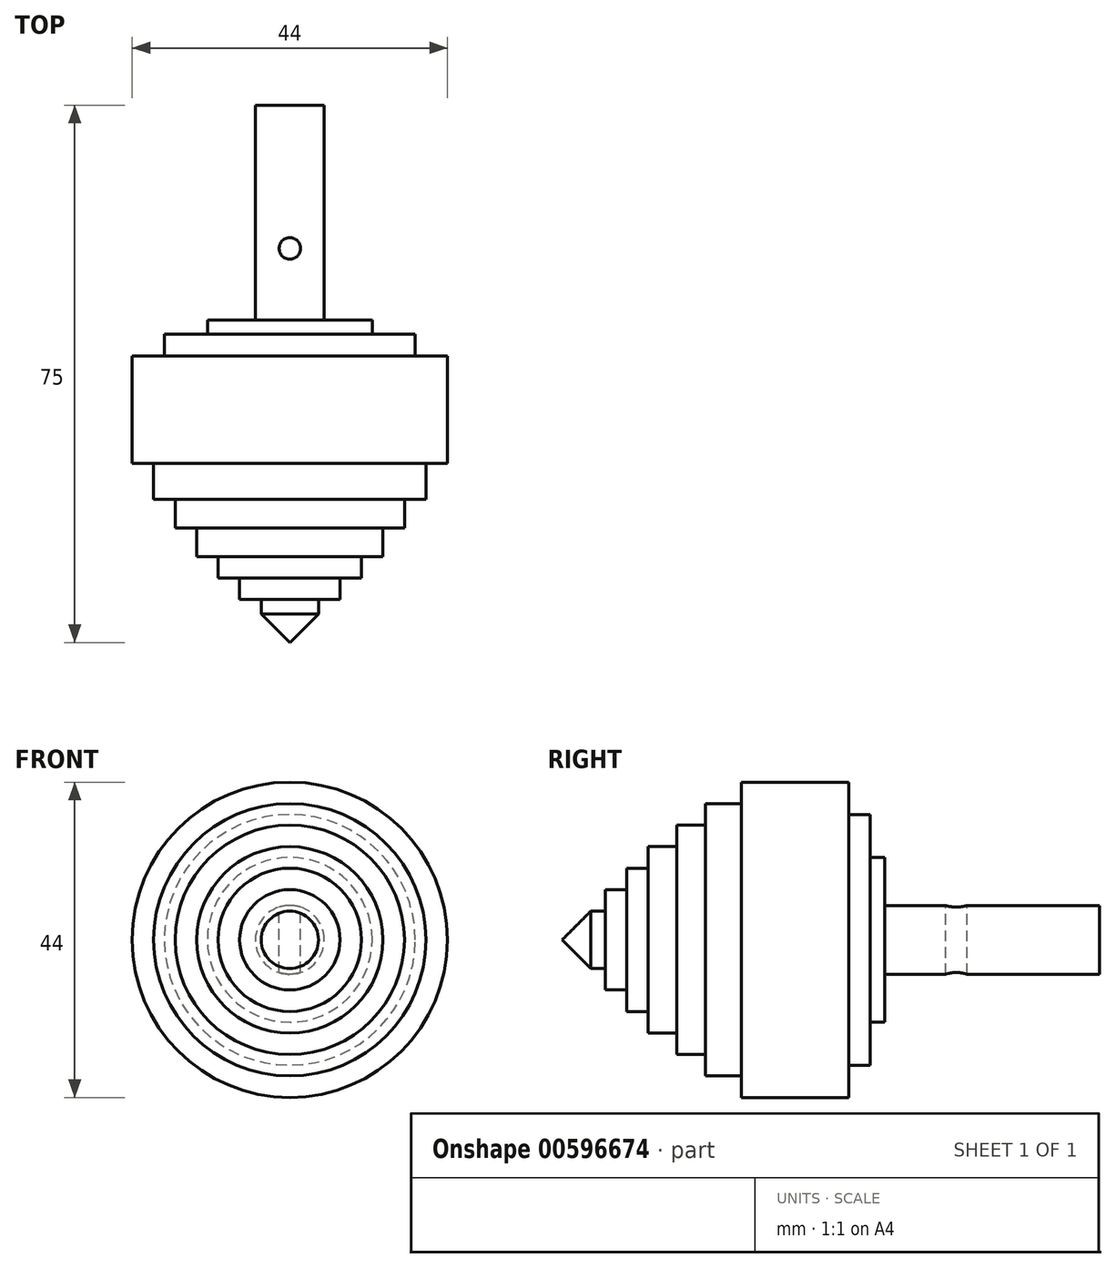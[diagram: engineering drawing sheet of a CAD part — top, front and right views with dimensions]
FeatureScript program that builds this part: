
annotation { "Feature Type Name" : "Feature", "Feature Type Description" : "" }
export const myFeature = defineFeature(function(context is Context, id is Id, definition is map)
    precondition{}
    {
        {
            var Q0;
            Q0=qCreatedBy(makeId("Front.planeOp"),FACE);
            var sketch = newSketch(context, id + "F0", { "sketchPlane" : qUnion([Q0])});
            skCircle(sketch, "E0", {"center": v(0, 0) * mm, "radius": 22 * mm});
            skCircle(sketch, "E1", {"center": v(0, 0) * mm, "radius": 19 * mm});
            skCircle(sketch, "E2", {"center": v(0, 0) * mm, "radius": 16 * mm});
            skCircle(sketch, "E3", {"center": v(0, 0) * mm, "radius": 13 * mm});
            skCircle(sketch, "E4", {"center": v(0, 0) * mm, "radius": 10 * mm});
            skCircle(sketch, "E5", {"center": v(0, 0) * mm, "radius": 7 * mm});
            skCircle(sketch, "E6", {"center": v(0, 0) * mm, "radius": 4 * mm});
            skSolve(sketch);
        }
        {
            var Q0;
            Q0 = qSketchRegion(id + "F0", true);
            var Q1;
            Q1=makeQuery(id+"F0.imprint","IMPRINT",FACE,{"disambiguationData":[TD([[makeQuery(id+"F0.imprint","IMPRINT",EDGE,{"derivedFrom":sQuery(id+"F0.wireOp",EDGE,"E1")}),1.0]])]});
            var Q2;
            Q2=makeQuery(id+"F0.imprint","IMPRINT",FACE,{"disambiguationData":[TD([[makeQuery(id+"F0.imprint","IMPRINT",EDGE,{"derivedFrom":sQuery(id+"F0.wireOp",EDGE,"E2")}),1.0]])]});
            var Q3;
            Q3=makeQuery(id+"F0.imprint","IMPRINT",FACE,{"disambiguationData":[TD([[makeQuery(id+"F0.imprint","IMPRINT",EDGE,{"derivedFrom":sQuery(id+"F0.wireOp",EDGE,"E3")}),1.0]])]});
            var Q4;
            Q4=makeQuery(id+"F0.imprint","IMPRINT",FACE,{"disambiguationData":[TD([[makeQuery(id+"F0.imprint","IMPRINT",EDGE,{"derivedFrom":sQuery(id+"F0.wireOp",EDGE,"E4")}),1.0]])]});
            var Q5;
            Q5=makeQuery(id+"F0.imprint","IMPRINT",FACE,{"disambiguationData":[TD([[makeQuery(id+"F0.imprint","IMPRINT",EDGE,{"derivedFrom":sQuery(id+"F0.wireOp",EDGE,"E5")}),1.0]])]});
            var Q6;
            Q6=makeQuery(id+"F0.imprint","IMPRINT",FACE,{"disambiguationData":[TD([[makeQuery(id+"F0.imprint","IMPRINT",EDGE,{"derivedFrom":sQuery(id+"F0.wireOp",EDGE,"E6")}),1.0]])]});
            extrude(context, id + "F1", {"entities" : qUnion([Q0, Q1, Q2, Q3, Q4, Q5, Q6]), "depth" : 15 * mm, "offsetDistance" : 25 * mm});
        }
        {
            var Q0;
            Q0=makeQuery(id+"F0.imprint","IMPRINT",FACE,{"disambiguationData":[TD([[makeQuery(id+"F0.imprint","IMPRINT",EDGE,{"derivedFrom":sQuery(id+"F0.wireOp",EDGE,"E1")}),1.0]])]});
            var Q1;
            Q1=makeQuery(id+"F0.imprint","IMPRINT",FACE,{"disambiguationData":[TD([[makeQuery(id+"F0.imprint","IMPRINT",EDGE,{"derivedFrom":sQuery(id+"F0.wireOp",EDGE,"E2")}),1.0]])]});
            var Q2;
            Q2=makeQuery(id+"F0.imprint","IMPRINT",FACE,{"disambiguationData":[TD([[makeQuery(id+"F0.imprint","IMPRINT",EDGE,{"derivedFrom":sQuery(id+"F0.wireOp",EDGE,"E3")}),1.0]])]});
            var Q3;
            Q3=makeQuery(id+"F0.imprint","IMPRINT",FACE,{"disambiguationData":[TD([[makeQuery(id+"F0.imprint","IMPRINT",EDGE,{"derivedFrom":sQuery(id+"F0.wireOp",EDGE,"E4")}),1.0]])]});
            var Q4;
            Q4=makeQuery(id+"F0.imprint","IMPRINT",FACE,{"disambiguationData":[TD([[makeQuery(id+"F0.imprint","IMPRINT",EDGE,{"derivedFrom":sQuery(id+"F0.wireOp",EDGE,"E5")}),1.0]])]});
            var Q5;
            Q5=makeQuery(id+"F0.imprint","IMPRINT",FACE,{"disambiguationData":[TD([[makeQuery(id+"F0.imprint","IMPRINT",EDGE,{"derivedFrom":sQuery(id+"F0.wireOp",EDGE,"E6")}),1.0]])]});
            extrude(context, id + "F2", {"entities" : qUnion([Q0, Q1, Q2, Q3, Q4, Q5]), "operationType" : NewBodyOperationType.ADD, "depth" : (15 + 5) * mm, "offsetDistance" : 25 * mm});
        }
        {
            var Q0;
            Q0=makeQuery(id+"F0.imprint","IMPRINT",FACE,{"disambiguationData":[TD([[makeQuery(id+"F0.imprint","IMPRINT",EDGE,{"derivedFrom":sQuery(id+"F0.wireOp",EDGE,"E2")}),1.0]])]});
            var Q1;
            Q1=makeQuery(id+"F0.imprint","IMPRINT",FACE,{"disambiguationData":[TD([[makeQuery(id+"F0.imprint","IMPRINT",EDGE,{"derivedFrom":sQuery(id+"F0.wireOp",EDGE,"E3")}),1.0]])]});
            var Q2;
            Q2=makeQuery(id+"F0.imprint","IMPRINT",FACE,{"disambiguationData":[TD([[makeQuery(id+"F0.imprint","IMPRINT",EDGE,{"derivedFrom":sQuery(id+"F0.wireOp",EDGE,"E4")}),1.0]])]});
            var Q3;
            Q3=makeQuery(id+"F0.imprint","IMPRINT",FACE,{"disambiguationData":[TD([[makeQuery(id+"F0.imprint","IMPRINT",EDGE,{"derivedFrom":sQuery(id+"F0.wireOp",EDGE,"E5")}),1.0]])]});
            var Q4;
            Q4=makeQuery(id+"F0.imprint","IMPRINT",FACE,{"disambiguationData":[TD([[makeQuery(id+"F0.imprint","IMPRINT",EDGE,{"derivedFrom":sQuery(id+"F0.wireOp",EDGE,"E6")}),1.0]])]});
            extrude(context, id + "F3", {"entities" : qUnion([Q0, Q1, Q2, Q3, Q4]), "operationType" : NewBodyOperationType.ADD, "depth" : (15 + 5 + 4) * mm, "offsetDistance" : 25 * mm});
        }
        {
            var Q0;
            Q0=makeQuery(id+"F0.imprint","IMPRINT",FACE,{"disambiguationData":[TD([[makeQuery(id+"F0.imprint","IMPRINT",EDGE,{"derivedFrom":sQuery(id+"F0.wireOp",EDGE,"E3")}),1.0]])]});
            var Q1;
            Q1=makeQuery(id+"F0.imprint","IMPRINT",FACE,{"disambiguationData":[TD([[makeQuery(id+"F0.imprint","IMPRINT",EDGE,{"derivedFrom":sQuery(id+"F0.wireOp",EDGE,"E4")}),1.0]])]});
            var Q2;
            Q2=makeQuery(id+"F0.imprint","IMPRINT",FACE,{"disambiguationData":[TD([[makeQuery(id+"F0.imprint","IMPRINT",EDGE,{"derivedFrom":sQuery(id+"F0.wireOp",EDGE,"E5")}),1.0]])]});
            var Q3;
            Q3=makeQuery(id+"F0.imprint","IMPRINT",FACE,{"disambiguationData":[TD([[makeQuery(id+"F0.imprint","IMPRINT",EDGE,{"derivedFrom":sQuery(id+"F0.wireOp",EDGE,"E6")}),1.0]])]});
            extrude(context, id + "F4", {"entities" : qUnion([Q0, Q1, Q2, Q3]), "operationType" : NewBodyOperationType.ADD, "depth" : (15 + 5 + 4 + 4) * mm, "offsetDistance" : 25 * mm});
        }
        {
            var Q0;
            Q0=makeQuery(id+"F0.imprint","IMPRINT",FACE,{"disambiguationData":[TD([[makeQuery(id+"F0.imprint","IMPRINT",EDGE,{"derivedFrom":sQuery(id+"F0.wireOp",EDGE,"E4")}),1.0]])]});
            var Q1;
            Q1=makeQuery(id+"F0.imprint","IMPRINT",FACE,{"disambiguationData":[TD([[makeQuery(id+"F0.imprint","IMPRINT",EDGE,{"derivedFrom":sQuery(id+"F0.wireOp",EDGE,"E5")}),1.0]])]});
            var Q2;
            Q2=makeQuery(id+"F0.imprint","IMPRINT",FACE,{"disambiguationData":[TD([[makeQuery(id+"F0.imprint","IMPRINT",EDGE,{"derivedFrom":sQuery(id+"F0.wireOp",EDGE,"E6")}),1.0]])]});
            extrude(context, id + "F5", {"entities" : qUnion([Q0, Q1, Q2]), "operationType" : NewBodyOperationType.ADD, "depth" : (15 + 5 + 4 + 4 + 3) * mm, "offsetDistance" : 25 * mm});
        }
        {
            var Q0;
            Q0=makeQuery(id+"F0.imprint","IMPRINT",FACE,{"disambiguationData":[TD([[makeQuery(id+"F0.imprint","IMPRINT",EDGE,{"derivedFrom":sQuery(id+"F0.wireOp",EDGE,"E5")}),1.0]])]});
            var Q1;
            Q1=makeQuery(id+"F0.imprint","IMPRINT",FACE,{"disambiguationData":[TD([[makeQuery(id+"F0.imprint","IMPRINT",EDGE,{"derivedFrom":sQuery(id+"F0.wireOp",EDGE,"E6")}),1.0]])]});
            extrude(context, id + "F6", {"entities" : qUnion([Q0, Q1]), "operationType" : NewBodyOperationType.ADD, "depth" : (15 + 5 + 4 + 4 + 3 + 3) * mm, "offsetDistance" : 25 * mm});
        }
        {
            var Q0;
            Q0=makeQuery(id+"F0.imprint","IMPRINT",FACE,{"disambiguationData":[TD([[makeQuery(id+"F0.imprint","IMPRINT",EDGE,{"derivedFrom":sQuery(id+"F0.wireOp",EDGE,"E6")}),1.0]])]});
            extrude(context, id + "F7", {"entities" : qUnion([Q0]), "operationType" : NewBodyOperationType.ADD, "depth" : (15 + 5 + 4 + 4 + 3 + 3 + 6) * mm, "offsetDistance" : 25 * mm});
        }
        {
            var Q0;
            Q0=makeQuery(id+"F7.opExtrude","CAP_EDGE",EDGE,{"disambiguationData":[OSD([sQuery(id+"F0.wireOp",EDGE,"E6")])],"isStart":false});
            chamfer(context, id + "F8", {"entities" : qUnion([Q0]), "width" : 4 * mm, "tangentPropagation" : true});
        }
        {
            var Q0;
            Q0=makeQuery(id+"F1.opExtrude","CAP_FACE",FACE,{"disambiguationData":[OSD([sQuery(id+"F0.wireOp",EDGE,"E0")])],"isStart":true});
            var sketch = newSketch(context, id + "F9", { "sketchPlane" : qUnion([Q0])});
            skCircle(sketch, "E7", {"center": v(0, 0) * mm, "radius": 17.5 * mm});
            skSolve(sketch);
        }
        {
            var Q0;
            Q0 = qSketchRegion(id + "F9", true);
            var Q1;
            Q1=makeQuery(id+"F9.imprint","IMPRINT",FACE,{"disambiguationData":[TD([[makeQuery(id+"F9.imprint","IMPRINT",EDGE,{"derivedFrom":sQuery(id+"F9.wireOp",EDGE,"npAo0AnT-dKzt-cCNW-4Sc1-pe3lxFMNtj5V")}),1.0]])]});
            var Q2;
            Q2=makeQuery(id+"F9.imprint","IMPRINT",FACE,{"disambiguationData":[TD([[makeQuery(id+"F9.imprint","IMPRINT",EDGE,{"derivedFrom":sQuery(id+"F9.wireOp",EDGE,"DGXihA1H-R8lH-G0iu-Yz30-3WSs6QrNYEyH")}),1.0]])]});
            extrude(context, id + "F10", {"entities" : qUnion([Q0, Q1, Q2]), "operationType" : NewBodyOperationType.ADD, "depth" : 3 * mm, "offsetDistance" : 25 * mm});
        }
        {
            var Q0;
            Q0=makeQuery(id+"F10.opExtrude","CAP_FACE",FACE,{"disambiguationData":[OSD([sQuery(id+"F9.wireOp",EDGE,"E7")])],"isStart":false});
            var sketch = newSketch(context, id + "F11", { "sketchPlane" : qUnion([Q0])});
            skCircle(sketch, "E8", {"center": v(0, 0) * mm, "radius": 11.5 * mm});
            skSolve(sketch);
        }
        {
            var Q0;
            Q0 = qSketchRegion(id + "F11", true);
            extrude(context, id + "F12", {"entities" : qUnion([Q0]), "operationType" : NewBodyOperationType.ADD, "depth" : 2 * mm, "offsetDistance" : 25 * mm});
        }
        {
            var Q0;
            Q0=makeQuery(id+"F12.opExtrude","CAP_FACE",FACE,{"disambiguationData":[OSD([sQuery(id+"F11.wireOp",EDGE,"E8")])],"isStart":false});
            var sketch = newSketch(context, id + "F13", { "sketchPlane" : qUnion([Q0])});
            skCircle(sketch, "E9", {"center": v(0, 0) * mm, "radius": 4.8 * mm});
            skSolve(sketch);
        }
        {
            var Q0;
            Q0 = qSketchRegion(id + "F13", true);
            extrude(context, id + "F14", {"entities" : qUnion([Q0]), "operationType" : NewBodyOperationType.ADD, "depth" : (75 - 40 - 5) * mm, "offsetDistance" : 25 * mm});
        }
        {
            var Q0;
            Q0=qCreatedBy(makeId("Top.planeOp"),FACE);
            var sketch = newSketch(context, id + "F15", { "sketchPlane" : qUnion([Q0])});
            skCircle(sketch, "E10", {"center": v(0, 15) * mm, "radius": 1.5 * mm});
            skSolve(sketch);
        }
        {
            var Q0;
            Q0 = qSketchRegion(id + "F15", true);
            extrude(context, id + "F16", {"entities" : qUnion([Q0]), "operationType" : NewBodyOperationType.REMOVE, "oppositeDirection" : true, "depth" : 25 * mm, "offsetDistance" : 25 * mm, "symmetric" : true});
        }
    });
